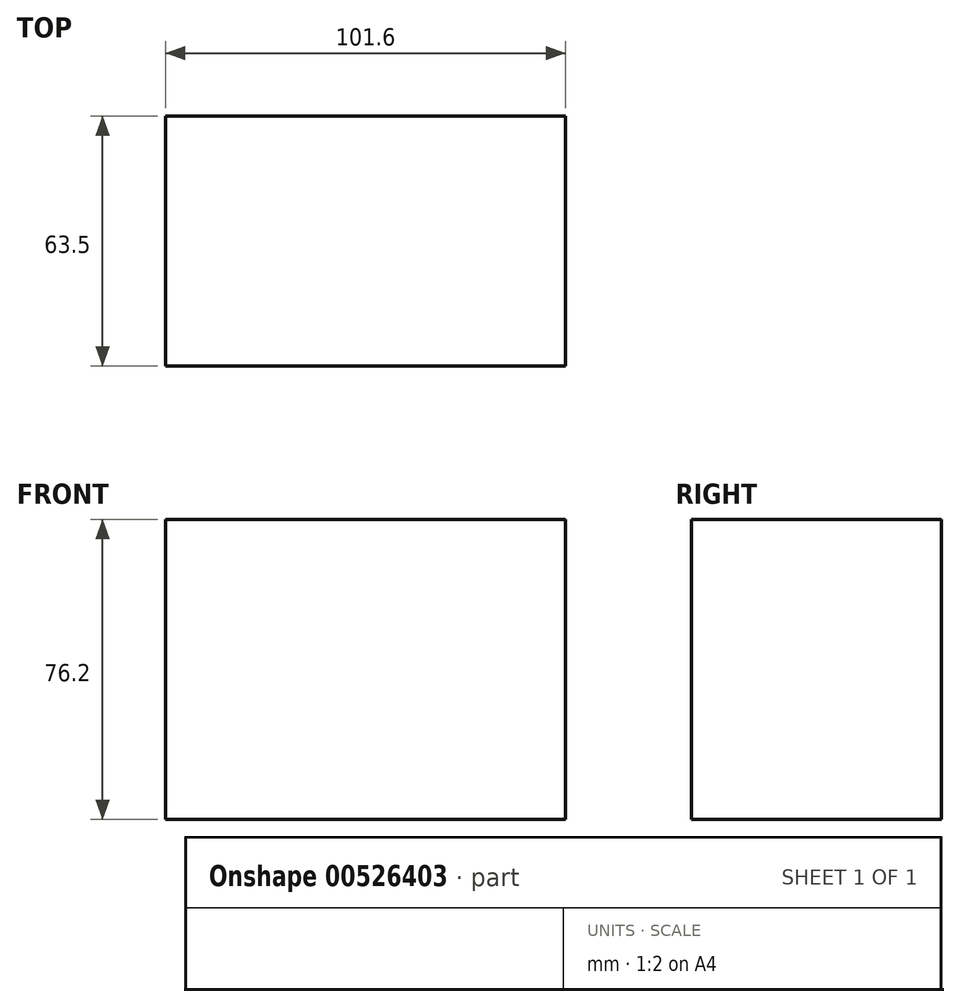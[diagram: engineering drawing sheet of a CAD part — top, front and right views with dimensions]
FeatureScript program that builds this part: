
annotation { "Feature Type Name" : "Feature", "Feature Type Description" : "" }
export const myFeature = defineFeature(function(context is Context, id is Id, definition is map)
    precondition{}
    {
        {
            var Q0;
            Q0=qCreatedBy(makeId("Top.planeOp"),FACE);
            var sketch = newSketch(context, id + "F0", { "sketchPlane" : qUnion([Q0])});
            skLineSegment(sketch, "E0.bottom", {"start": v(0, 0) * mm, "end": v(101.6, 0) * mm});
            skLineSegment(sketch, "E0.top", {"start": v(0, -63.5) * mm, "end": v(101.6, -63.5) * mm});
            skLineSegment(sketch, "E0.left", {"start": v(0, 0) * mm, "end": v(0, -63.5) * mm});
            skLineSegment(sketch, "E0.right", {"start": v(101.6, 0) * mm, "end": v(101.6, -63.5) * mm});
            skSolve(sketch);
        }
        {
            var Q0;
            Q0=makeQuery(id+"F0.imprint","IMPRINT",FACE,{"disambiguationData":[TD([[makeQuery(id+"F0.imprint","IMPRINT",EDGE,{"derivedFrom":sQuery(id+"F0.wireOp",EDGE,"E0.bottom")}),-1.0]])]});
            extrude(context, id + "F1", {"entities" : qUnion([Q0]), "depth" : 76.2 * mm, "offsetDistance" : 25.4 * mm});
        }
    });
